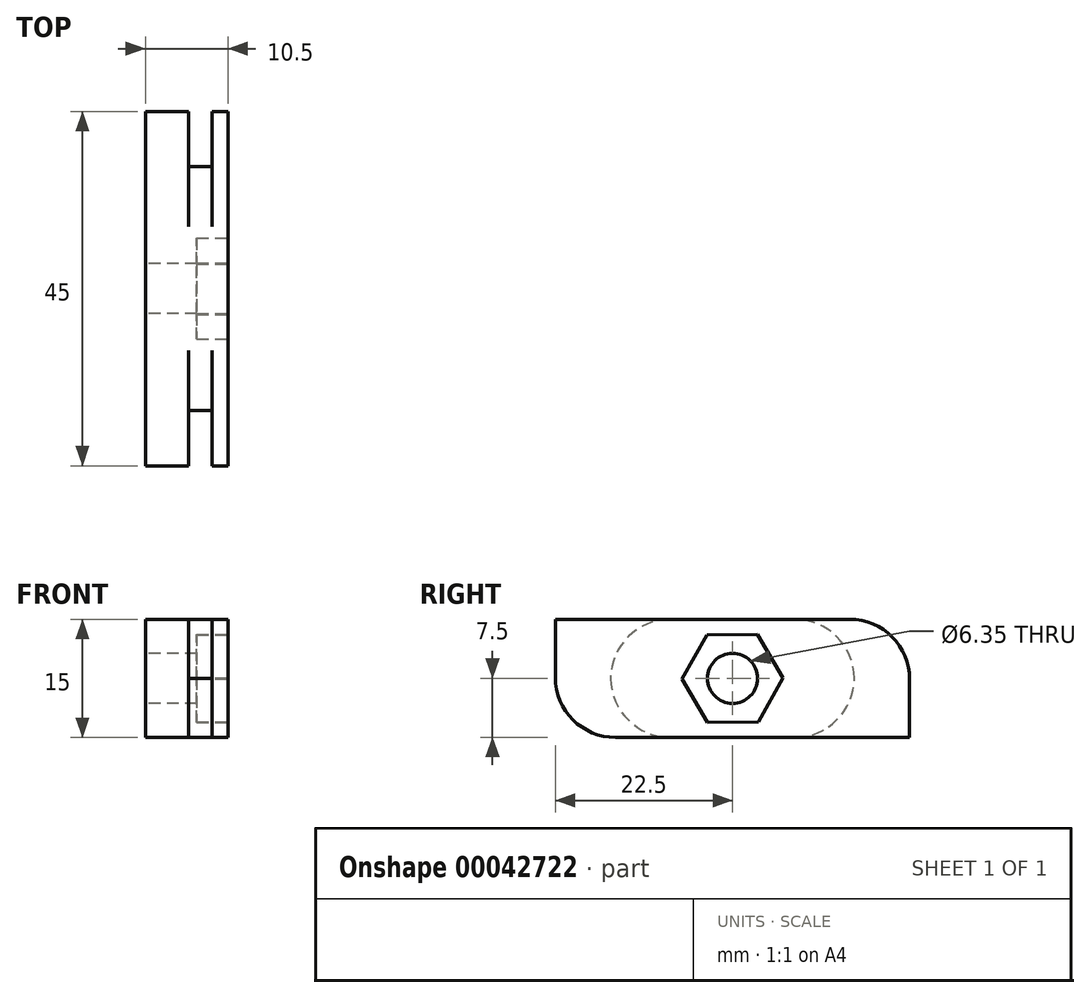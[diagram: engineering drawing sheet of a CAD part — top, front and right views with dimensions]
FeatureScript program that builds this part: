
annotation { "Feature Type Name" : "Feature", "Feature Type Description" : "" }
export const myFeature = defineFeature(function(context is Context, id is Id, definition is map)
    precondition{}
    {
        {
            var Q0;
            Q0=qCreatedBy(makeId("Top.planeOp"),FACE);
            var sketch = newSketch(context, id + "F0", { "sketchPlane" : qUnion([Q0])});
            skLineSegment(sketch, "E0.top", {"start": v(-23.46, -7) * mm, "end": v(-17.96, -7) * mm});
            skLineSegment(sketch, "E0.left", {"start": v(-23.46, 38) * mm, "end": v(-23.46, -7) * mm});
            skLineSegment(sketch, "E0.right", {"start": v(-12.96, 38) * mm, "end": v(-12.96, -7) * mm});
            skLineSegment(sketch, "E1", {"start": v(-12.96, 38) * mm, "end": v(-14.96, 38) * mm, "construction": true});
            skLineSegment(sketch, "E2", {"start": v(-14.96, 38) * mm, "end": v(-17.96, 38) * mm, "construction": true});
            skLineSegment(sketch, "E3", {"start": v(-23.46, 38) * mm, "end": v(-17.96, 38) * mm});
            skLineSegment(sketch, "E4", {"start": v(-17.96, 38) * mm, "end": v(-17.96, 31) * mm});
            skLineSegment(sketch, "E5", {"start": v(-17.96, 31) * mm, "end": v(-14.96, 31) * mm});
            skLineSegment(sketch, "E6", {"start": v(-14.96, 38) * mm, "end": v(-14.96, 31) * mm});
            skLineSegment(sketch, "E7", {"start": v(-14.96, 38) * mm, "end": v(-12.96, 38) * mm});
            skLineSegment(sketch, "E8", {"start": v(-17.96, 31) * mm, "end": v(-17.96, -19.5) * mm, "construction": true});
            skLineSegment(sketch, "E9", {"start": v(-17.96, -19.5) * mm, "end": v(-11.99, -19.5) * mm, "construction": true});
            skLineSegment(sketch, "E10", {"start": v(-14.96, 31) * mm, "end": v(-14.96, -19.5) * mm, "construction": true});
            skLineSegment(sketch, "E11", {"start": v(-17.96, -7) * mm, "end": v(-17.96, 0) * mm});
            skLineSegment(sketch, "E12", {"start": v(-17.96, 0) * mm, "end": v(-14.96, 0) * mm});
            skLineSegment(sketch, "E13", {"start": v(-14.96, 0) * mm, "end": v(-14.96, -7) * mm});
            skLineSegment(sketch, "E14.trimOffspring", {"start": v(-14.96, -7) * mm, "end": v(-12.96, -7) * mm});
            skSolve(sketch);
        }
        {
            var Q0;
            Q0=makeQuery(id+"F0.imprint","IMPRINT",FACE,{"disambiguationData":[TD([[makeQuery(id+"F0.imprint","IMPRINT",EDGE,{"derivedFrom":sQuery(id+"F0.wireOp",EDGE,"E0.top")}),1.0]])]});
            extrude(context, id + "F1", {"entities" : qUnion([Q0]), "depth" : 15 * mm});
        }
        {
            var Q0;
            Q0=makeQuery(id+"F1.opExtrude","SWEPT_FACE",FACE,{"disambiguationData":[OSD([sQuery(id+"F0.wireOp",EDGE,"E0.left")])]});
            var sketch = newSketch(context, id + "F2", { "sketchPlane" : qUnion([Q0])});
            skLineSegment(sketch, "E15", {"start": v(-38, 15) * mm, "end": v(7, 0) * mm, "construction": true});
            skLineSegment(sketch, "E16", {"start": v(7, 0) * mm, "end": v(7, 15) * mm, "construction": true});
            skLineSegment(sketch, "E17", {"start": v(7, 15) * mm, "end": v(-38, 0) * mm, "construction": true});
            skCircle(sketch, "E18", {"center": v(-15.5, 7.5) * mm, "radius": 1.95 * mm, "construction": true});
            skCircle(sketch, "E19", {"center": v(-15.5, 7.5) * mm, "radius": 3.18 * mm});
            skSolve(sketch);
        }
        {
            var Q0;
            Q0=makeQuery(id+"F2.imprint","IMPRINT",FACE,{"disambiguationData":[TD([[makeQuery(id+"F2.imprint","IMPRINT",EDGE,{"derivedFrom":sQuery(id+"F2.wireOp",EDGE,"E19")}),1.0]])]});
            var Q1;
            Q1=sQuery(id+"F2.wireOp",EDGE,"E19");
            extrude(context, id + "F3", {"entities" : qUnion([Q0]), "operationType" : NewBodyOperationType.REMOVE, "surfaceEntities" : qUnion([Q1]), "oppositeDirection" : true, "depth" : 25.4 * mm});
        }
        {
            var Q0;
            Q0=makeQuery(id+"F1.opExtrude","SWEPT_FACE",FACE,{"disambiguationData":[OSD([sQuery(id+"F0.wireOp",EDGE,"E0.right")])]});
            var sketch = newSketch(context, id + "F4", { "sketchPlane" : qUnion([Q0])});
            skCircle(sketch, "E20.cCircle", {"center": v(15.5, 7.5) * mm, "radius": 5.56 * mm, "construction": true});
            skLineSegment(sketch, "E20.0", {"start": v(18.65, 13.09) * mm, "end": v(21.92, 7.57) * mm});
            skLineSegment(sketch, "E20.1", {"start": v(21.92, 7.57) * mm, "end": v(18.77, 1.98) * mm});
            skLineSegment(sketch, "E20.2", {"start": v(18.77, 1.98) * mm, "end": v(12.35, 1.91) * mm});
            skLineSegment(sketch, "E20.3", {"start": v(12.35, 1.91) * mm, "end": v(9.08, 7.43) * mm});
            skLineSegment(sketch, "E20.4", {"start": v(9.08, 7.43) * mm, "end": v(12.23, 13.02) * mm});
            skLineSegment(sketch, "E20.5", {"start": v(12.23, 13.02) * mm, "end": v(18.65, 13.09) * mm});
            skPoint(sketch, "E20.0.midPoint", {"position": v(20.28, 10.33) * mm});
            skSolve(sketch);
        }
        {
            var Q0;
            Q0=makeQuery(id+"F4.imprint","IMPRINT",FACE,{"disambiguationData":[TD([[makeQuery(id+"F4.imprint","IMPRINT",EDGE,{"derivedFrom":sQuery(id+"F4.wireOp",EDGE,"E20.0")}),-1.0]])]});
            extrude(context, id + "F5", {"entities" : qUnion([Q0]), "operationType" : NewBodyOperationType.REMOVE, "oppositeDirection" : true, "depth" : 3.97 * mm});
        }
        {
            var Q0;
            Q0=makeQuery(id+"F1.opExtrude","CAP_EDGE",EDGE,{"disambiguationData":[OSD([sQuery(id+"F0.wireOp",EDGE,"E12")])],"isStart":false});
            var Q1;
            Q1=makeQuery(id+"F1.opExtrude","CAP_EDGE",EDGE,{"disambiguationData":[OSD([sQuery(id+"F0.wireOp",EDGE,"E5")])],"isStart":false});
            var Q2;
            Q2=makeQuery(id+"F1.opExtrude","CAP_EDGE",EDGE,{"disambiguationData":[OSD([sQuery(id+"F0.wireOp",EDGE,"E12")])],"isStart":true});
            var Q3;
            Q3=makeQuery(id+"F1.opExtrude","CAP_EDGE",EDGE,{"disambiguationData":[OSD([sQuery(id+"F0.wireOp",EDGE,"E5")])],"isStart":true});
            fillet(context, id + "F6", {"entities" : qUnion([Q0, Q1, Q2, Q3]), "radius" : 7.62 * mm, "tangentPropagation" : true, "allowEdgeOverflow" : false});
        }
        {
            var Q0;
            Q0=makeQuery(id+"F1.opExtrude","CAP_EDGE",EDGE,{"disambiguationData":[OSD([sQuery(id+"F0.wireOp",EDGE,"E7")])],"isStart":false});
            var Q1;
            Q1=makeQuery(id+"F1.opExtrude","CAP_EDGE",EDGE,{"disambiguationData":[OSD([sQuery(id+"F0.wireOp",EDGE,"E14.trimOffspring")])],"isStart":true});
            var Q2;
            Q2=makeQuery(id+"F1.opExtrude","CAP_EDGE",EDGE,{"disambiguationData":[OSD([sQuery(id+"F0.wireOp",EDGE,"E0.top")])],"isStart":true});
            var Q3;
            Q3=makeQuery(id+"F1.opExtrude","CAP_EDGE",EDGE,{"disambiguationData":[OSD([sQuery(id+"F0.wireOp",EDGE,"E3")])],"isStart":false});
            fillet(context, id + "F7", {"entities" : qUnion([Q0, Q1, Q2, Q3]), "radius" : 7.62 * mm, "tangentPropagation" : true, "allowEdgeOverflow" : false});
        }
    });
